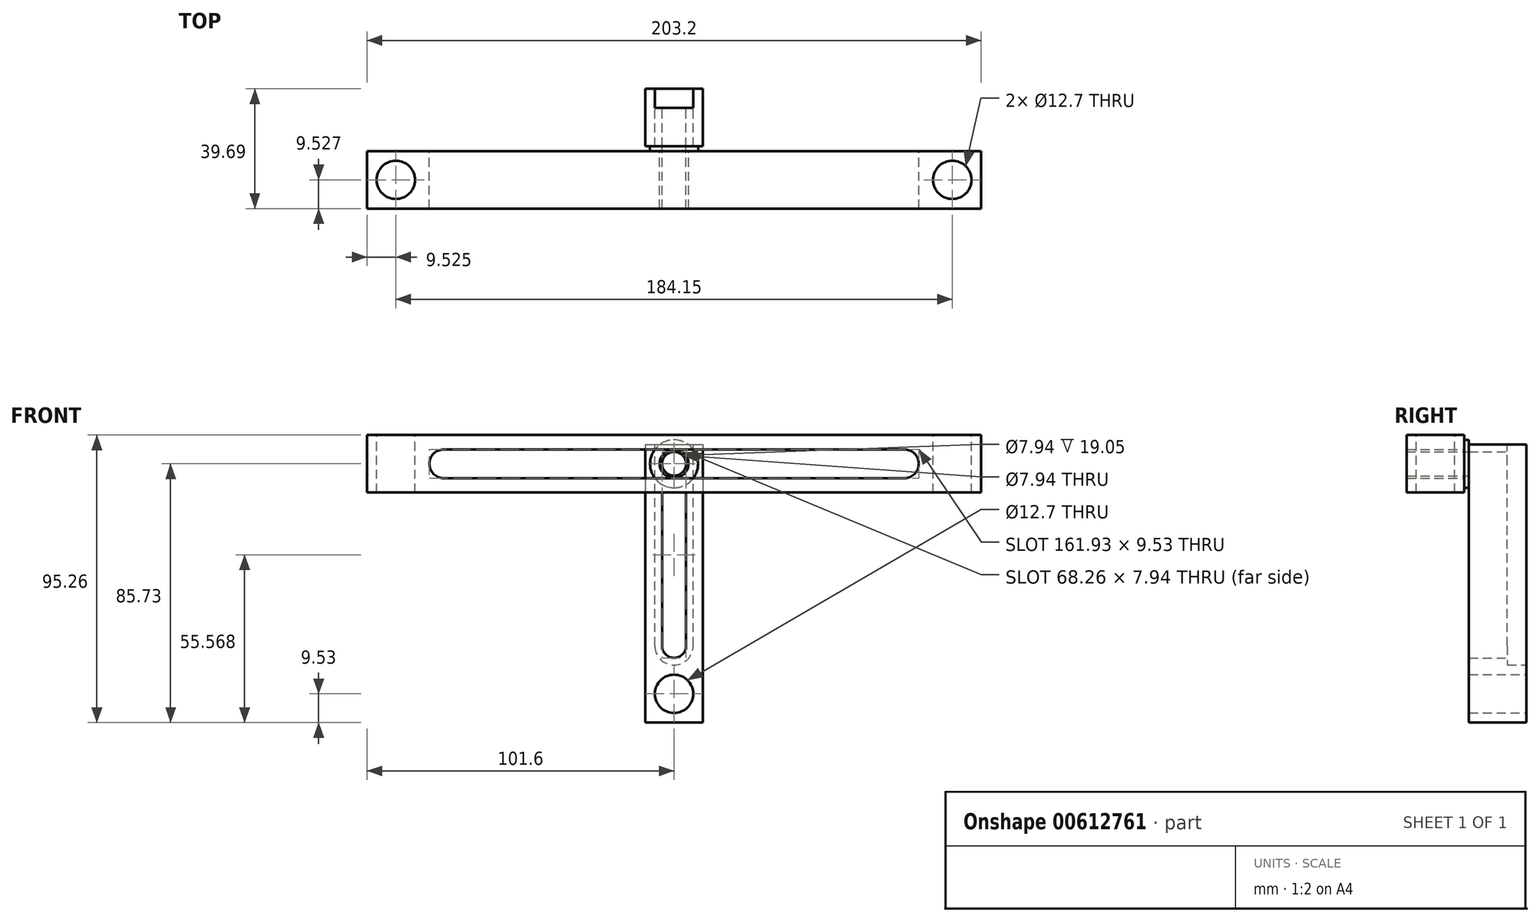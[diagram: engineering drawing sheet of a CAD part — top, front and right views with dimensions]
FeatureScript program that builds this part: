
annotation { "Feature Type Name" : "Feature", "Feature Type Description" : "" }
export const myFeature = defineFeature(function(context is Context, id is Id, definition is map)
    precondition{}
    {
        {
            var Q0;
            Q0=qCreatedBy(makeId("Front.planeOp"),FACE);
            var sketch = newSketch(context, id + "F0", { "sketchPlane" : qUnion([Q0])});
            skCircle(sketch, "E0", {"center": v(0, 0) * mm, "radius": 6.35 * mm});
            skLineSegment(sketch, "E1.bottom", {"start": v(-9.53, 82.55) * mm, "end": v(9.52, 82.55) * mm});
            skLineSegment(sketch, "E1.top", {"start": v(-9.52, -9.53) * mm, "end": v(9.53, -9.53) * mm});
            skLineSegment(sketch, "E1.left", {"start": v(-9.52, 82.55) * mm, "end": v(-9.52, -9.53) * mm});
            skLineSegment(sketch, "E1.right", {"start": v(9.53, 82.55) * mm, "end": v(9.53, -9.53) * mm});
            skLineSegment(sketch, "E2", {"start": v(9.53, 9.52) * mm, "end": v(-9.52, 9.52) * mm, "construction": true});
            skLineSegment(sketch, "E3", {"start": v(-9.52, 9.52) * mm, "end": v(9.53, -9.53) * mm, "construction": true});
            skArc(sketch, "E4", {"start": v(3.97, 76.2) * mm, "mid": v(0, 80.17) * mm, "end": v(-3.97, 76.2) * mm});
            skArc(sketch, "E5", {"start": v(-3.97, 15.88) * mm, "mid": v(0, 11.9) * mm, "end": v(3.97, 15.88) * mm});
            skLineSegment(sketch, "E6", {"start": v(-3.97, 76.2) * mm, "end": v(-3.97, 15.88) * mm});
            skLineSegment(sketch, "E7", {"start": v(3.97, 76.2) * mm, "end": v(3.97, 15.88) * mm});
            skSolve(sketch);
        }
        {
            var Q0;
            Q0 = qSketchRegion(id + "F0", true);
            extrude(context, id + "F1", {"entities" : qUnion([Q0]), "depth" : 19.05 * mm, "offsetDistance" : 25.4 * mm});
        }
        {
            var Q0;
            Q0=makeQuery(id+"F1.opExtrude","CAP_FACE",FACE,{"disambiguationData":[OSD([sQuery(id+"F0.wireOp",EDGE,"E0"),sQuery(id+"F0.wireOp",EDGE,"E1.bottom"),sQuery(id+"F0.wireOp",EDGE,"E1.top"),sQuery(id+"F0.wireOp",EDGE,"E1.left"),sQuery(id+"F0.wireOp",EDGE,"E1.right"),sQuery(id+"F0.wireOp",EDGE,"E4"),sQuery(id+"F0.wireOp",EDGE,"E5"),sQuery(id+"F0.wireOp",EDGE,"E6"),sQuery(id+"F0.wireOp",EDGE,"E7")])],"isStart":true});
            var sketch = newSketch(context, id + "F2", { "sketchPlane" : qUnion([Q0])});
            skLineSegment(sketch, "E8", {"start": v(-6.35, 0) * mm, "end": v(6.35, 0) * mm, "construction": true});
            skPoint(sketch, "E9", {"position": v(0, 0) * mm});
            skLineSegment(sketch, "E10", {"start": v(6.35, 15.88) * mm, "end": v(6.35, 82.55) * mm});
            skLineSegment(sketch, "E11", {"start": v(-6.35, 15.88) * mm, "end": v(-6.35, 82.55) * mm});
            skArc(sketch, "E12", {"start": v(-6.35, 15.88) * mm, "mid": v(0, 9.52) * mm, "end": v(6.35, 15.88) * mm});
            skLineSegment(sketch, "E13", {"start": v(-6.35, 82.55) * mm, "end": v(6.35, 82.55) * mm});
            skSolve(sketch);
        }
        {
            var Q0;
            Q0 = qSketchRegion(id + "F2", true);
            extrude(context, id + "F3", {"entities" : qUnion([Q0]), "operationType" : NewBodyOperationType.REMOVE, "oppositeDirection" : true, "depth" : 6.35 * mm, "offsetDistance" : 25.4 * mm});
        }
        {
            var Q0;
            Q0=makeQuery(id+"F1.opExtrude","CAP_FACE",FACE,{"disambiguationData":[OSD([sQuery(id+"F0.wireOp",EDGE,"E0"),sQuery(id+"F0.wireOp",EDGE,"E1.bottom"),sQuery(id+"F0.wireOp",EDGE,"E1.top"),sQuery(id+"F0.wireOp",EDGE,"E1.left"),sQuery(id+"F0.wireOp",EDGE,"E1.right"),sQuery(id+"F0.wireOp",EDGE,"E4"),sQuery(id+"F0.wireOp",EDGE,"E5"),sQuery(id+"F0.wireOp",EDGE,"E6"),sQuery(id+"F0.wireOp",EDGE,"E7")])],"isStart":false});
            var sketch = newSketch(context, id + "F4", { "sketchPlane" : qUnion([Q0])});
            skCircle(sketch, "E14", {"center": v(0, 76.2) * mm, "radius": 3.97 * mm});
            skCircle(sketch, "E15", {"center": v(0, 76.2) * mm, "radius": 7.94 * mm});
            skSolve(sketch);
        }
        {
            var Q0;
            Q0 = qSketchRegion(id + "F4", true);
            extrude(context, id + "F5", {"entities" : qUnion([Q0]), "depth" : 1.59 * mm, "offsetDistance" : 25.4 * mm});
        }
        {
            var Q0;
            Q0=makeQuery(id+"F5.opExtrude","CAP_FACE",FACE,{"disambiguationData":[OSD([sQuery(id+"F4.wireOp",EDGE,"E14"),sQuery(id+"F4.wireOp",EDGE,"E15")])],"isStart":false});
            var sketch = newSketch(context, id + "F6", { "sketchPlane" : qUnion([Q0])});
            skCircle(sketch, "E16", {"center": v(0, 76.2) * mm, "radius": 4.76 * mm});
            skCircle(sketch, "E17", {"center": v(0, 76.2) * mm, "radius": 3.97 * mm});
            skSolve(sketch);
        }
        {
            var Q0;
            Q0 = qSketchRegion(id + "F6", true);
            extrude(context, id + "F7", {"entities" : qUnion([Q0]), "depth" : 19.05 * mm, "offsetDistance" : 25.4 * mm});
        }
        {
            var Q0;
            Q0=makeQuery(id+"F5.opExtrude","CAP_FACE",FACE,{"disambiguationData":[OSD([sQuery(id+"F4.wireOp",EDGE,"E14"),sQuery(id+"F4.wireOp",EDGE,"E15")])],"isStart":false});
            var sketch = newSketch(context, id + "F8", { "sketchPlane" : qUnion([Q0])});
            skLineSegment(sketch, "E18.bottom", {"start": v(-101.6, 85.72) * mm, "end": v(101.6, 85.72) * mm});
            skLineSegment(sketch, "E18.top", {"start": v(-101.6, 66.67) * mm, "end": v(101.6, 66.67) * mm});
            skLineSegment(sketch, "E18.left", {"start": v(-101.6, 85.72) * mm, "end": v(-101.6, 66.67) * mm});
            skLineSegment(sketch, "E18.right", {"start": v(101.6, 85.72) * mm, "end": v(101.6, 66.67) * mm});
            skLineSegment(sketch, "E19", {"start": v(-101.6, 85.72) * mm, "end": v(101.6, 66.67) * mm, "construction": true});
            skPoint(sketch, "E20", {"position": v(0, 76.2) * mm});
            skLineSegment(sketch, "E21", {"start": v(-76.2, 76.2) * mm, "end": v(76.2, 76.2) * mm, "construction": true});
            skArc(sketch, "E22", {"start": v(-76.2, 80.96) * mm, "mid": v(-80.96, 76.2) * mm, "end": v(-76.2, 71.44) * mm});
            skArc(sketch, "E23", {"start": v(76.2, 71.44) * mm, "mid": v(80.96, 76.2) * mm, "end": v(76.2, 80.96) * mm});
            skLineSegment(sketch, "E24", {"start": v(-76.2, 71.44) * mm, "end": v(76.2, 71.44) * mm});
            skLineSegment(sketch, "E25.trimOffspring", {"start": v(-76.2, 80.96) * mm, "end": v(76.2, 80.96) * mm});
            skSolve(sketch);
        }
        {
            var Q0;
            Q0 = qSketchRegion(id + "F8", true);
            extrude(context, id + "F9", {"entities" : qUnion([Q0]), "depth" : 19.05 * mm, "offsetDistance" : 25.4 * mm});
        }
        {
            var Q0;
            Q0=makeQuery(id+"F9.opExtrude","SWEPT_FACE",FACE,{"disambiguationData":[OSD([sQuery(id+"F8.wireOp",EDGE,"E18.bottom")])]});
            var sketch = newSketch(context, id + "F10", { "sketchPlane" : qUnion([Q0])});
            skCircle(sketch, "E26", {"center": v(-92.07, -30.16) * mm, "radius": 6.35 * mm});
            skCircle(sketch, "E27", {"center": v(92.08, -30.16) * mm, "radius": 6.35 * mm});
            skLineSegment(sketch, "E28", {"start": v(-82.55, -20.64) * mm, "end": v(-82.55, -39.69) * mm, "construction": true});
            skLineSegment(sketch, "E29", {"start": v(-101.6, -20.64) * mm, "end": v(-82.55, -20.64) * mm, "construction": true});
            skLineSegment(sketch, "E30", {"start": v(-101.6, -20.64) * mm, "end": v(-82.55, -39.69) * mm, "construction": true});
            skLineSegment(sketch, "E31", {"start": v(82.55, -39.69) * mm, "end": v(82.55, -20.64) * mm, "construction": true});
            skLineSegment(sketch, "E32", {"start": v(82.55, -20.64) * mm, "end": v(101.6, -20.64) * mm, "construction": true});
            skLineSegment(sketch, "E33", {"start": v(101.6, -20.64) * mm, "end": v(82.55, -39.69) * mm, "construction": true});
            skSolve(sketch);
        }
        {
            var Q0;
            Q0 = qSketchRegion(id + "F10", true);
            extrude(context, id + "F11", {"entities" : qUnion([Q0]), "operationType" : NewBodyOperationType.REMOVE, "endBound" : BoundingType.UP_TO_NEXT, "oppositeDirection" : true, "depth" : 25.4 * mm, "offsetDistance" : 25.4 * mm});
        }
    });
